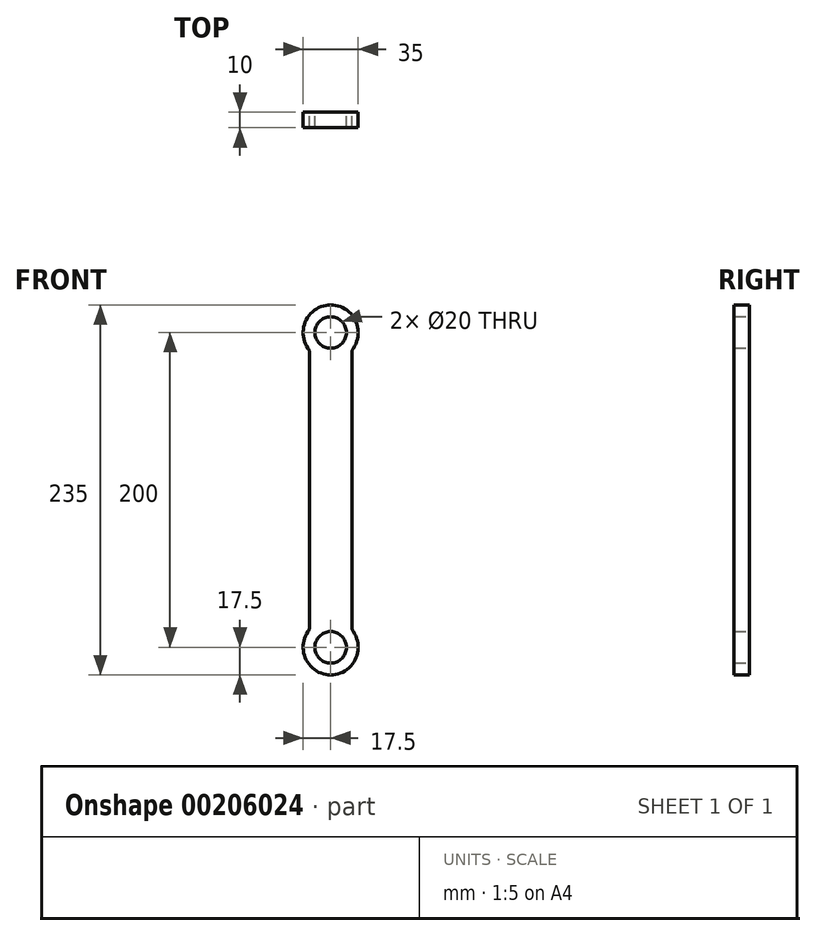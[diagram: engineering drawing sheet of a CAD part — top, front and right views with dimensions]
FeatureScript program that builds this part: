
annotation { "Feature Type Name" : "Feature", "Feature Type Description" : "" }
export const myFeature = defineFeature(function(context is Context, id is Id, definition is map)
    precondition{}
    {
        {
            var Q0;
            Q0=qCreatedBy(makeId("Front.planeOp"),FACE);
            var sketch = newSketch(context, id + "F0", { "sketchPlane" : qUnion([Q0])});
            skCircle(sketch, "E0", {"center": v(0, 0) * mm, "radius": 10 * mm});
            skCircle(sketch, "E1", {"center": v(0, 200) * mm, "radius": 10 * mm});
            skLineSegment(sketch, "E2.left", {"start": v(0, 0) * mm, "end": v(0, 200) * mm});
            skArc(sketch, "E3", {"start": v(14.33, 189.96) * mm, "mid": v(0, 217.5) * mm, "end": v(-14.33, 189.96) * mm});
            skArc(sketch, "E4", {"start": v(-14.33, 10.04) * mm, "mid": v(0, -17.5) * mm, "end": v(14.33, 10.04) * mm});
            skLineSegment(sketch, "E5.trimOffspring", {"start": v(-13.43, 12.9) * mm, "end": v(-13.43, 187.1) * mm});
            skLineSegment(sketch, "E6.trimOffspring", {"start": v(13.43, 12.9) * mm, "end": v(13.43, 187.1) * mm});
            skPoint(sketch, "E7.visualSharp", {"position": v(13.43, 188.78) * mm});
            skArc(sketch, "E7.filletArc", {"start": v(14.33, 189.96) * mm, "mid": v(13.66, 188.6) * mm, "end": v(13.43, 187.1) * mm});
            skPoint(sketch, "E8.visualSharp", {"position": v(-13.43, 188.78) * mm});
            skArc(sketch, "E8.filletArc", {"start": v(-13.43, 187.1) * mm, "mid": v(-13.66, 188.6) * mm, "end": v(-14.33, 189.96) * mm});
            skPoint(sketch, "E9.visualSharp", {"position": v(-13.43, 11.22) * mm});
            skArc(sketch, "E9.filletArc", {"start": v(-14.33, 10.04) * mm, "mid": v(-13.66, 11.4) * mm, "end": v(-13.43, 12.9) * mm});
            skPoint(sketch, "E10.visualSharp", {"position": v(13.43, 11.22) * mm});
            skArc(sketch, "E10.filletArc", {"start": v(13.43, 12.9) * mm, "mid": v(13.66, 11.4) * mm, "end": v(14.33, 10.04) * mm});
            skSolve(sketch);
        }
        {
            var Q0;
            Q0=makeQuery(id+"F0.imprint","IMPRINT",FACE,{"disambiguationData":[TD([[makeQuery(id+"F0.imprint","IMPRINT",EDGE,{"derivedFrom":sQuery(id+"F0.wireOp",EDGE,"E0")}),-1.0]])]});
            extrude(context, id + "F1", {"entities" : qUnion([Q0]), "depth" : 10 * mm});
        }
    });
